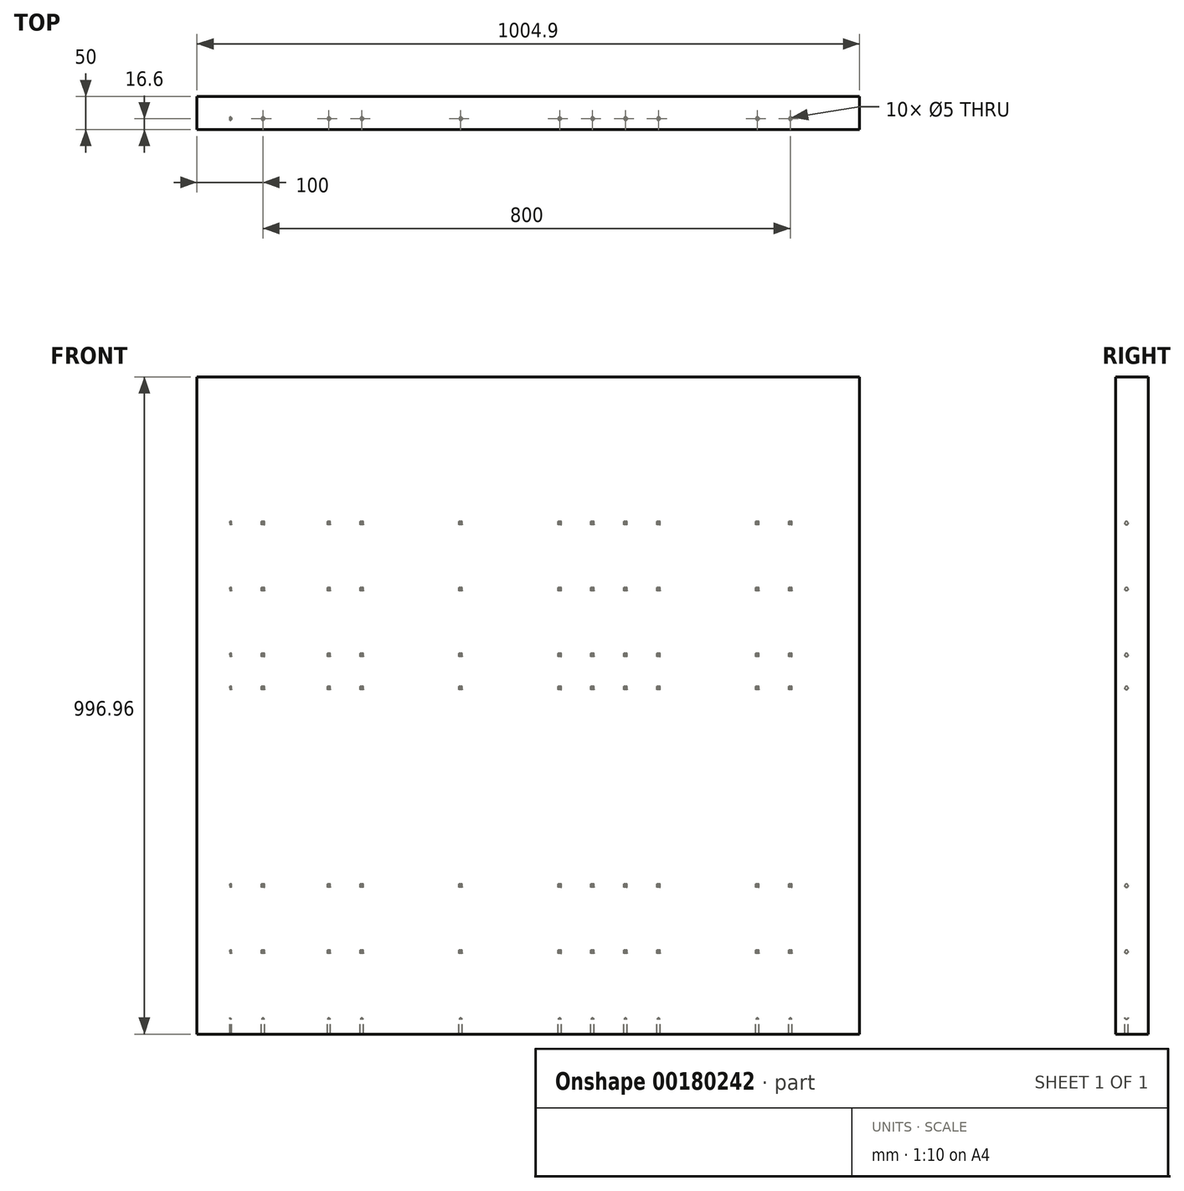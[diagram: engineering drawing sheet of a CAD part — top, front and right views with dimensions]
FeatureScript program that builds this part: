
annotation { "Feature Type Name" : "Feature", "Feature Type Description" : "" }
export const myFeature = defineFeature(function(context is Context, id is Id, definition is map)
    precondition{}
    {
        {
            var Q0;
            Q0=qCreatedBy(makeId("Right.planeOp"),FACE);
            var sketch = newSketch(context, id + "F0", { "sketchPlane" : qUnion([Q0])});
            skLineSegment(sketch, "E0.bottom", {"start": v(25, 491.35) * mm, "end": v(-25, 491.35) * mm});
            skLineSegment(sketch, "E0.top", {"start": v(25, -505.6) * mm, "end": v(-25, -505.6) * mm});
            skLineSegment(sketch, "E0.left", {"start": v(25, 491.35) * mm, "end": v(25, -505.6) * mm});
            skLineSegment(sketch, "E0.right", {"start": v(-25, 491.35) * mm, "end": v(-25, -505.6) * mm});
            skPoint(sketch, "E0.middle", {"position": v(0, -7.13) * mm});
            skLineSegment(sketch, "E1.0", {"start": v(25, -480.6) * mm, "end": v(-25, -480.6) * mm});
            skLineSegment(sketch, "E2.0", {"start": v(-8.4, 542.15) * mm, "end": v(-8.4, -505.6) * mm});
            skCircle(sketch, "E3", {"center": v(-8.4, -480.6) * mm, "radius": 2.5 * mm});
            skCircle(sketch, "E4.0.1.0", {"center": v(-8.4, -430.6) * mm, "radius": 2.5 * mm});
            skCircle(sketch, "E4.0.2.0", {"center": v(-8.4, -380.6) * mm, "radius": 2.5 * mm});
            skCircle(sketch, "E4.0.3.0", {"center": v(-8.4, -330.6) * mm, "radius": 2.5 * mm});
            skCircle(sketch, "E4.0.4.0", {"center": v(-8.4, -280.6) * mm, "radius": 2.5 * mm});
            skCircle(sketch, "E4.0.5.0", {"center": v(-8.4, -230.6) * mm, "radius": 2.5 * mm});
            skCircle(sketch, "E4.0.6.0", {"center": v(-8.4, -180.6) * mm, "radius": 2.5 * mm});
            skCircle(sketch, "E4.0.7.0", {"center": v(-8.4, -130.6) * mm, "radius": 2.5 * mm});
            skCircle(sketch, "E4.0.8.0", {"center": v(-8.4, -80.6) * mm, "radius": 2.5 * mm});
            skCircle(sketch, "E4.0.9.0", {"center": v(-8.4, -30.6) * mm, "radius": 2.5 * mm});
            skCircle(sketch, "E4.0.10.0", {"center": v(-8.4, 19.4) * mm, "radius": 2.5 * mm});
            skCircle(sketch, "E4.0.11.0", {"center": v(-8.4, 69.4) * mm, "radius": 2.5 * mm});
            skCircle(sketch, "E4.0.12.0", {"center": v(-8.4, 119.4) * mm, "radius": 2.5 * mm});
            skCircle(sketch, "E4.0.13.0", {"center": v(-8.4, 169.4) * mm, "radius": 2.5 * mm});
            skCircle(sketch, "E4.0.14.0", {"center": v(-8.4, 219.4) * mm, "radius": 2.5 * mm});
            skCircle(sketch, "E4.0.15.0", {"center": v(-8.4, 269.4) * mm, "radius": 2.5 * mm});
            skCircle(sketch, "E4.0.16.0", {"center": v(-8.4, 319.4) * mm, "radius": 2.5 * mm});
            skCircle(sketch, "E4.0.17.0", {"center": v(-8.4, 369.4) * mm, "radius": 2.5 * mm});
            skCircle(sketch, "E4.0.18.0", {"center": v(-8.4, 419.4) * mm, "radius": 2.5 * mm});
            skLineSegment(sketch, "E4.direction1", {"start": v(-8.4, -480.6) * mm, "end": v(16.6, -480.6) * mm, "construction": true});
            skLineSegment(sketch, "E4.direction2", {"start": v(-8.4, -480.6) * mm, "end": v(-8.4, -430.6) * mm, "construction": true});
            skLineSegment(sketch, "E5", {"start": v(0, 0) * mm, "end": v(63.1, 0) * mm});
            skSolve(sketch);
        }
        {
            var Q0;
            Q0=qCreatedBy(makeId("Top.planeOp"),FACE);
            cPlane(context, id + "F1", {"entities" : qUnion([Q0]), "cplaneType" : CPlaneType.OFFSET, "offset" : 431.2 * mm, "width" : 150 * mm, "height" : 150 * mm});
        }
        {
            var Q0;
            Q0=qCreatedBy(id+"F1.planeOp",FACE);
            var sketch = newSketch(context, id + "F2", { "sketchPlane" : qUnion([Q0])});
            skLineSegment(sketch, "E6.bottom", {"start": v(1004.9, -25) * mm, "end": v(0, -25) * mm});
            skLineSegment(sketch, "E6.top", {"start": v(1004.9, 25) * mm, "end": v(0, 25) * mm});
            skLineSegment(sketch, "E6.left", {"start": v(1004.9, -25) * mm, "end": v(1004.9, 25) * mm});
            skLineSegment(sketch, "E6.right", {"start": v(0, -25) * mm, "end": v(0, 25) * mm});
            skPoint(sketch, "E6.middle", {"position": v(502.45, 0) * mm});
            skLineSegment(sketch, "E7", {"start": v(0, 25) * mm, "end": v(51.84, 25) * mm});
            skLineSegment(sketch, "E8", {"start": v(0, 25) * mm, "end": v(0, 69.64) * mm});
            skLineSegment(sketch, "E9.0", {"start": v(1004.9, -8.4) * mm, "end": v(0, -8.4) * mm});
            skLineSegment(sketch, "E10.0", {"start": v(50, -25) * mm, "end": v(50, 25) * mm});
            skCircle(sketch, "E11", {"center": v(50, -8.4) * mm, "radius": 2.5 * mm});
            skCircle(sketch, "E12.1.0.0", {"center": v(100, -8.4) * mm, "radius": 2.5 * mm});
            skCircle(sketch, "E12.2.0.0", {"center": v(150, -8.4) * mm, "radius": 2.5 * mm});
            skCircle(sketch, "E12.3.0.0", {"center": v(200, -8.4) * mm, "radius": 2.5 * mm});
            skCircle(sketch, "E12.4.0.0", {"center": v(250, -8.4) * mm, "radius": 2.5 * mm});
            skCircle(sketch, "E12.5.0.0", {"center": v(300, -8.4) * mm, "radius": 2.5 * mm});
            skCircle(sketch, "E12.6.0.0", {"center": v(350, -8.4) * mm, "radius": 2.5 * mm});
            skCircle(sketch, "E12.7.0.0", {"center": v(400, -8.4) * mm, "radius": 2.5 * mm});
            skCircle(sketch, "E12.8.0.0", {"center": v(450, -8.4) * mm, "radius": 2.5 * mm});
            skCircle(sketch, "E12.9.0.0", {"center": v(500, -8.4) * mm, "radius": 2.5 * mm});
            skCircle(sketch, "E12.10.0.0", {"center": v(550, -8.4) * mm, "radius": 2.5 * mm});
            skCircle(sketch, "E12.11.0.0", {"center": v(600, -8.4) * mm, "radius": 2.5 * mm});
            skCircle(sketch, "E12.12.0.0", {"center": v(650, -8.4) * mm, "radius": 2.5 * mm});
            skCircle(sketch, "E12.13.0.0", {"center": v(700, -8.4) * mm, "radius": 2.5 * mm});
            skCircle(sketch, "E12.14.0.0", {"center": v(750, -8.4) * mm, "radius": 2.5 * mm});
            skCircle(sketch, "E12.15.0.0", {"center": v(800, -8.4) * mm, "radius": 2.5 * mm});
            skCircle(sketch, "E12.16.0.0", {"center": v(850, -8.4) * mm, "radius": 2.5 * mm});
            skCircle(sketch, "E12.17.0.0", {"center": v(900, -8.4) * mm, "radius": 2.5 * mm});
            skCircle(sketch, "E12.18.0.0", {"center": v(950, -8.4) * mm, "radius": 2.5 * mm});
            skLineSegment(sketch, "E12.direction1", {"start": v(50, -8.4) * mm, "end": v(100, -8.4) * mm, "construction": true});
            skSolve(sketch);
        }
        {
            var Q0;
            {var subQ0=sQuery(id+"F0.wireOp",EDGE,"E4.0.18.0");var subQ1=sQuery(id+"F0.wireOp",EDGE,"E2.0");var subQ2=makeQuery(id+"F0.imprint","INTERSECT",VERTEX,{"disambiguationData":[OD(0.0)],"derivedFrom":[subQ1,subQ0]});Q0=makeQuery(id+"F0.imprint","IMPRINT",FACE,{"disambiguationData":[TD([[makeQuery(id+"F0.imprint","IMPRINT",EDGE,{"disambiguationData":[TD([[subQ2,-1.0]])],"derivedFrom":subQ1}),-1.0]])]});}
            var Q1;
            {var subQ0=sQuery(id+"F0.wireOp",EDGE,"E4.0.19.0");var subQ1=sQuery(id+"F0.wireOp",EDGE,"E2.0");var subQ2=makeQuery(id+"F0.imprint","INTERSECT",VERTEX,{"disambiguationData":[OD(0.0)],"derivedFrom":[subQ1,subQ0]});Q1=makeQuery(id+"F0.imprint","IMPRINT",FACE,{"disambiguationData":[TD([[makeQuery(id+"F0.imprint","IMPRINT",EDGE,{"disambiguationData":[TD([[subQ2,-1.0]])],"derivedFrom":subQ1}),1.0]])]});}
            var Q2;
            {var subQ0=sQuery(id+"F0.wireOp",EDGE,"E4.0.19.0");var subQ1=sQuery(id+"F0.wireOp",EDGE,"E2.0");var subQ2=makeQuery(id+"F0.imprint","INTERSECT",VERTEX,{"disambiguationData":[OD(0.0)],"derivedFrom":[subQ1,subQ0]});Q2=makeQuery(id+"F0.imprint","IMPRINT",FACE,{"disambiguationData":[TD([[makeQuery(id+"F0.imprint","IMPRINT",EDGE,{"disambiguationData":[TD([[subQ2,-1.0]])],"derivedFrom":subQ1}),-1.0]])]});}
            var Q3;
            {var subQ0=sQuery(id+"F0.wireOp",EDGE,"E4.0.17.0");var subQ1=sQuery(id+"F0.wireOp",EDGE,"E2.0");var subQ2=makeQuery(id+"F0.imprint","INTERSECT",VERTEX,{"disambiguationData":[OD(0.0)],"derivedFrom":[subQ1,subQ0]});Q3=makeQuery(id+"F0.imprint","IMPRINT",FACE,{"disambiguationData":[TD([[makeQuery(id+"F0.imprint","IMPRINT",EDGE,{"disambiguationData":[TD([[subQ2,-1.0]])],"derivedFrom":subQ1}),1.0]])]});}
            var Q4;
            {var subQ0=sQuery(id+"F0.wireOp",EDGE,"E4.0.17.0");var subQ1=sQuery(id+"F0.wireOp",EDGE,"E2.0");var subQ2=makeQuery(id+"F0.imprint","INTERSECT",VERTEX,{"disambiguationData":[OD(0.0)],"derivedFrom":[subQ1,subQ0]});Q4=makeQuery(id+"F0.imprint","IMPRINT",FACE,{"disambiguationData":[TD([[makeQuery(id+"F0.imprint","IMPRINT",EDGE,{"disambiguationData":[TD([[subQ2,-1.0]])],"derivedFrom":subQ1}),-1.0]])]});}
            var Q5;
            {var subQ0=sQuery(id+"F0.wireOp",EDGE,"E4.0.18.0");var subQ1=sQuery(id+"F0.wireOp",EDGE,"E2.0");var subQ2=makeQuery(id+"F0.imprint","INTERSECT",VERTEX,{"disambiguationData":[OD(0.0)],"derivedFrom":[subQ1,subQ0]});Q5=makeQuery(id+"F0.imprint","IMPRINT",FACE,{"disambiguationData":[TD([[makeQuery(id+"F0.imprint","IMPRINT",EDGE,{"disambiguationData":[TD([[subQ2,-1.0]])],"derivedFrom":subQ1}),1.0]])]});}
            var Q6;
            {var subQ0=sQuery(id+"F0.wireOp",EDGE,"E4.0.16.0");var subQ1=sQuery(id+"F0.wireOp",EDGE,"E2.0");var subQ2=makeQuery(id+"F0.imprint","INTERSECT",VERTEX,{"disambiguationData":[OD(0.0)],"derivedFrom":[subQ1,subQ0]});Q6=makeQuery(id+"F0.imprint","IMPRINT",FACE,{"disambiguationData":[TD([[makeQuery(id+"F0.imprint","IMPRINT",EDGE,{"disambiguationData":[TD([[subQ2,-1.0]])],"derivedFrom":subQ1}),1.0]])]});}
            var Q7;
            {var subQ0=sQuery(id+"F0.wireOp",EDGE,"E4.0.16.0");var subQ1=sQuery(id+"F0.wireOp",EDGE,"E2.0");var subQ2=makeQuery(id+"F0.imprint","INTERSECT",VERTEX,{"disambiguationData":[OD(0.0)],"derivedFrom":[subQ1,subQ0]});Q7=makeQuery(id+"F0.imprint","IMPRINT",FACE,{"disambiguationData":[TD([[makeQuery(id+"F0.imprint","IMPRINT",EDGE,{"disambiguationData":[TD([[subQ2,-1.0]])],"derivedFrom":subQ1}),-1.0]])]});}
            var Q8;
            {var subQ0=sQuery(id+"F0.wireOp",EDGE,"E4.0.15.0");var subQ1=sQuery(id+"F0.wireOp",EDGE,"E2.0");var subQ2=makeQuery(id+"F0.imprint","INTERSECT",VERTEX,{"disambiguationData":[OD(0.0)],"derivedFrom":[subQ1,subQ0]});Q8=makeQuery(id+"F0.imprint","IMPRINT",FACE,{"disambiguationData":[TD([[makeQuery(id+"F0.imprint","IMPRINT",EDGE,{"disambiguationData":[TD([[subQ2,-1.0]])],"derivedFrom":subQ1}),1.0]])]});}
            var Q9;
            {var subQ0=sQuery(id+"F0.wireOp",EDGE,"E4.0.14.0");var subQ1=sQuery(id+"F0.wireOp",EDGE,"E2.0");var subQ2=makeQuery(id+"F0.imprint","INTERSECT",VERTEX,{"disambiguationData":[OD(0.0)],"derivedFrom":[subQ1,subQ0]});Q9=makeQuery(id+"F0.imprint","IMPRINT",FACE,{"disambiguationData":[TD([[makeQuery(id+"F0.imprint","IMPRINT",EDGE,{"disambiguationData":[TD([[subQ2,-1.0]])],"derivedFrom":subQ1}),-1.0]])]});}
            var Q10;
            {var subQ0=sQuery(id+"F0.wireOp",EDGE,"E4.0.15.0");var subQ1=sQuery(id+"F0.wireOp",EDGE,"E2.0");var subQ2=makeQuery(id+"F0.imprint","INTERSECT",VERTEX,{"disambiguationData":[OD(0.0)],"derivedFrom":[subQ1,subQ0]});Q10=makeQuery(id+"F0.imprint","IMPRINT",FACE,{"disambiguationData":[TD([[makeQuery(id+"F0.imprint","IMPRINT",EDGE,{"disambiguationData":[TD([[subQ2,-1.0]])],"derivedFrom":subQ1}),-1.0]])]});}
            var Q11;
            {var subQ0=sQuery(id+"F0.wireOp",EDGE,"E4.0.13.0");var subQ1=sQuery(id+"F0.wireOp",EDGE,"E2.0");var subQ2=makeQuery(id+"F0.imprint","INTERSECT",VERTEX,{"disambiguationData":[OD(0.0)],"derivedFrom":[subQ1,subQ0]});Q11=makeQuery(id+"F0.imprint","IMPRINT",FACE,{"disambiguationData":[TD([[makeQuery(id+"F0.imprint","IMPRINT",EDGE,{"disambiguationData":[TD([[subQ2,-1.0]])],"derivedFrom":subQ1}),1.0]])]});}
            var Q12;
            {var subQ0=sQuery(id+"F0.wireOp",EDGE,"E4.0.14.0");var subQ1=sQuery(id+"F0.wireOp",EDGE,"E2.0");var subQ2=makeQuery(id+"F0.imprint","INTERSECT",VERTEX,{"disambiguationData":[OD(0.0)],"derivedFrom":[subQ1,subQ0]});Q12=makeQuery(id+"F0.imprint","IMPRINT",FACE,{"disambiguationData":[TD([[makeQuery(id+"F0.imprint","IMPRINT",EDGE,{"disambiguationData":[TD([[subQ2,-1.0]])],"derivedFrom":subQ1}),1.0]])]});}
            var Q13;
            {var subQ0=sQuery(id+"F0.wireOp",EDGE,"E4.0.13.0");var subQ1=sQuery(id+"F0.wireOp",EDGE,"E2.0");var subQ2=makeQuery(id+"F0.imprint","INTERSECT",VERTEX,{"disambiguationData":[OD(0.0)],"derivedFrom":[subQ1,subQ0]});Q13=makeQuery(id+"F0.imprint","IMPRINT",FACE,{"disambiguationData":[TD([[makeQuery(id+"F0.imprint","IMPRINT",EDGE,{"disambiguationData":[TD([[subQ2,-1.0]])],"derivedFrom":subQ1}),-1.0]])]});}
            var Q14;
            {var subQ0=sQuery(id+"F0.wireOp",EDGE,"E4.0.9.0");var subQ1=sQuery(id+"F0.wireOp",EDGE,"E2.0");var subQ2=makeQuery(id+"F0.imprint","INTERSECT",VERTEX,{"disambiguationData":[OD(0.0)],"derivedFrom":[subQ1,subQ0]});Q14=makeQuery(id+"F0.imprint","IMPRINT",FACE,{"disambiguationData":[TD([[makeQuery(id+"F0.imprint","IMPRINT",EDGE,{"disambiguationData":[TD([[subQ2,-1.0]])],"derivedFrom":subQ1}),1.0]])]});}
            var Q15;
            {var subQ0=sQuery(id+"F0.wireOp",EDGE,"E4.0.9.0");var subQ1=sQuery(id+"F0.wireOp",EDGE,"E2.0");var subQ2=makeQuery(id+"F0.imprint","INTERSECT",VERTEX,{"disambiguationData":[OD(0.0)],"derivedFrom":[subQ1,subQ0]});Q15=makeQuery(id+"F0.imprint","IMPRINT",FACE,{"disambiguationData":[TD([[makeQuery(id+"F0.imprint","IMPRINT",EDGE,{"disambiguationData":[TD([[subQ2,-1.0]])],"derivedFrom":subQ1}),-1.0]])]});}
            var Q16;
            {var subQ0=sQuery(id+"F0.wireOp",EDGE,"E4.0.10.0");var subQ1=sQuery(id+"F0.wireOp",EDGE,"E2.0");var subQ2=makeQuery(id+"F0.imprint","INTERSECT",VERTEX,{"disambiguationData":[OD(0.0)],"derivedFrom":[subQ1,subQ0]});Q16=makeQuery(id+"F0.imprint","IMPRINT",FACE,{"disambiguationData":[TD([[makeQuery(id+"F0.imprint","IMPRINT",EDGE,{"disambiguationData":[TD([[subQ2,-1.0]])],"derivedFrom":subQ1}),-1.0]])]});}
            var Q17;
            {var subQ0=sQuery(id+"F0.wireOp",EDGE,"E4.0.12.0");var subQ1=sQuery(id+"F0.wireOp",EDGE,"E2.0");var subQ2=makeQuery(id+"F0.imprint","INTERSECT",VERTEX,{"disambiguationData":[OD(0.0)],"derivedFrom":[subQ1,subQ0]});Q17=makeQuery(id+"F0.imprint","IMPRINT",FACE,{"disambiguationData":[TD([[makeQuery(id+"F0.imprint","IMPRINT",EDGE,{"disambiguationData":[TD([[subQ2,-1.0]])],"derivedFrom":subQ1}),1.0]])]});}
            var Q18;
            {var subQ0=sQuery(id+"F0.wireOp",EDGE,"E4.0.6.0");var subQ1=sQuery(id+"F0.wireOp",EDGE,"E2.0");var subQ2=makeQuery(id+"F0.imprint","INTERSECT",VERTEX,{"disambiguationData":[OD(0.0)],"derivedFrom":[subQ1,subQ0]});Q18=makeQuery(id+"F0.imprint","IMPRINT",FACE,{"disambiguationData":[TD([[makeQuery(id+"F0.imprint","IMPRINT",EDGE,{"disambiguationData":[TD([[subQ2,-1.0]])],"derivedFrom":subQ1}),-1.0]])]});}
            var Q19;
            {var subQ0=sQuery(id+"F0.wireOp",EDGE,"E4.0.11.0");var subQ1=sQuery(id+"F0.wireOp",EDGE,"E2.0");var subQ2=makeQuery(id+"F0.imprint","INTERSECT",VERTEX,{"disambiguationData":[OD(0.0)],"derivedFrom":[subQ1,subQ0]});Q19=makeQuery(id+"F0.imprint","IMPRINT",FACE,{"disambiguationData":[TD([[makeQuery(id+"F0.imprint","IMPRINT",EDGE,{"disambiguationData":[TD([[subQ2,-1.0]])],"derivedFrom":subQ1}),1.0]])]});}
            var Q20;
            {var subQ0=sQuery(id+"F0.wireOp",EDGE,"E4.0.10.0");var subQ1=sQuery(id+"F0.wireOp",EDGE,"E2.0");var subQ2=makeQuery(id+"F0.imprint","INTERSECT",VERTEX,{"disambiguationData":[OD(0.0)],"derivedFrom":[subQ1,subQ0]});Q20=makeQuery(id+"F0.imprint","IMPRINT",FACE,{"disambiguationData":[TD([[makeQuery(id+"F0.imprint","IMPRINT",EDGE,{"disambiguationData":[TD([[subQ2,-1.0]])],"derivedFrom":subQ1}),1.0]])]});}
            var Q21;
            {var subQ0=sQuery(id+"F0.wireOp",EDGE,"E4.0.7.0");var subQ1=sQuery(id+"F0.wireOp",EDGE,"E2.0");var subQ2=makeQuery(id+"F0.imprint","INTERSECT",VERTEX,{"disambiguationData":[OD(0.0)],"derivedFrom":[subQ1,subQ0]});Q21=makeQuery(id+"F0.imprint","IMPRINT",FACE,{"disambiguationData":[TD([[makeQuery(id+"F0.imprint","IMPRINT",EDGE,{"disambiguationData":[TD([[subQ2,-1.0]])],"derivedFrom":subQ1}),-1.0]])]});}
            var Q22;
            {var subQ0=sQuery(id+"F0.wireOp",EDGE,"E4.0.8.0");var subQ1=sQuery(id+"F0.wireOp",EDGE,"E2.0");var subQ2=makeQuery(id+"F0.imprint","INTERSECT",VERTEX,{"disambiguationData":[OD(0.0)],"derivedFrom":[subQ1,subQ0]});Q22=makeQuery(id+"F0.imprint","IMPRINT",FACE,{"disambiguationData":[TD([[makeQuery(id+"F0.imprint","IMPRINT",EDGE,{"disambiguationData":[TD([[subQ2,-1.0]])],"derivedFrom":subQ1}),-1.0]])]});}
            var Q23;
            {var subQ0=sQuery(id+"F0.wireOp",EDGE,"E4.0.11.0");var subQ1=sQuery(id+"F0.wireOp",EDGE,"E2.0");var subQ2=makeQuery(id+"F0.imprint","INTERSECT",VERTEX,{"disambiguationData":[OD(0.0)],"derivedFrom":[subQ1,subQ0]});Q23=makeQuery(id+"F0.imprint","IMPRINT",FACE,{"disambiguationData":[TD([[makeQuery(id+"F0.imprint","IMPRINT",EDGE,{"disambiguationData":[TD([[subQ2,-1.0]])],"derivedFrom":subQ1}),-1.0]])]});}
            var Q24;
            {var subQ0=sQuery(id+"F0.wireOp",EDGE,"E4.0.12.0");var subQ1=sQuery(id+"F0.wireOp",EDGE,"E2.0");var subQ2=makeQuery(id+"F0.imprint","INTERSECT",VERTEX,{"disambiguationData":[OD(0.0)],"derivedFrom":[subQ1,subQ0]});Q24=makeQuery(id+"F0.imprint","IMPRINT",FACE,{"disambiguationData":[TD([[makeQuery(id+"F0.imprint","IMPRINT",EDGE,{"disambiguationData":[TD([[subQ2,-1.0]])],"derivedFrom":subQ1}),-1.0]])]});}
            var Q25;
            {var subQ0=sQuery(id+"F0.wireOp",EDGE,"E4.0.6.0");var subQ1=sQuery(id+"F0.wireOp",EDGE,"E2.0");var subQ2=makeQuery(id+"F0.imprint","INTERSECT",VERTEX,{"disambiguationData":[OD(0.0)],"derivedFrom":[subQ1,subQ0]});Q25=makeQuery(id+"F0.imprint","IMPRINT",FACE,{"disambiguationData":[TD([[makeQuery(id+"F0.imprint","IMPRINT",EDGE,{"disambiguationData":[TD([[subQ2,-1.0]])],"derivedFrom":subQ1}),1.0]])]});}
            var Q26;
            {var subQ0=sQuery(id+"F0.wireOp",EDGE,"E4.0.7.0");var subQ1=sQuery(id+"F0.wireOp",EDGE,"E2.0");var subQ2=makeQuery(id+"F0.imprint","INTERSECT",VERTEX,{"disambiguationData":[OD(0.0)],"derivedFrom":[subQ1,subQ0]});Q26=makeQuery(id+"F0.imprint","IMPRINT",FACE,{"disambiguationData":[TD([[makeQuery(id+"F0.imprint","IMPRINT",EDGE,{"disambiguationData":[TD([[subQ2,-1.0]])],"derivedFrom":subQ1}),1.0]])]});}
            var Q27;
            {var subQ0=sQuery(id+"F0.wireOp",EDGE,"E4.0.8.0");var subQ1=sQuery(id+"F0.wireOp",EDGE,"E2.0");var subQ2=makeQuery(id+"F0.imprint","INTERSECT",VERTEX,{"disambiguationData":[OD(0.0)],"derivedFrom":[subQ1,subQ0]});Q27=makeQuery(id+"F0.imprint","IMPRINT",FACE,{"disambiguationData":[TD([[makeQuery(id+"F0.imprint","IMPRINT",EDGE,{"disambiguationData":[TD([[subQ2,-1.0]])],"derivedFrom":subQ1}),1.0]])]});}
            var Q28;
            {var subQ0=sQuery(id+"F0.wireOp",EDGE,"E4.0.3.0");var subQ1=sQuery(id+"F0.wireOp",EDGE,"E2.0");var subQ2=makeQuery(id+"F0.imprint","INTERSECT",VERTEX,{"disambiguationData":[OD(0.0)],"derivedFrom":[subQ1,subQ0]});Q28=makeQuery(id+"F0.imprint","IMPRINT",FACE,{"disambiguationData":[TD([[makeQuery(id+"F0.imprint","IMPRINT",EDGE,{"disambiguationData":[TD([[subQ2,-1.0]])],"derivedFrom":subQ1}),-1.0]])]});}
            var Q29;
            {var subQ0=sQuery(id+"F0.wireOp",EDGE,"E4.0.4.0");var subQ1=sQuery(id+"F0.wireOp",EDGE,"E2.0");var subQ2=makeQuery(id+"F0.imprint","INTERSECT",VERTEX,{"disambiguationData":[OD(0.0)],"derivedFrom":[subQ1,subQ0]});Q29=makeQuery(id+"F0.imprint","IMPRINT",FACE,{"disambiguationData":[TD([[makeQuery(id+"F0.imprint","IMPRINT",EDGE,{"disambiguationData":[TD([[subQ2,-1.0]])],"derivedFrom":subQ1}),-1.0]])]});}
            var Q30;
            {var subQ0=sQuery(id+"F0.wireOp",EDGE,"E4.0.3.0");var subQ1=sQuery(id+"F0.wireOp",EDGE,"E2.0");var subQ2=makeQuery(id+"F0.imprint","INTERSECT",VERTEX,{"disambiguationData":[OD(0.0)],"derivedFrom":[subQ1,subQ0]});Q30=makeQuery(id+"F0.imprint","IMPRINT",FACE,{"disambiguationData":[TD([[makeQuery(id+"F0.imprint","IMPRINT",EDGE,{"disambiguationData":[TD([[subQ2,-1.0]])],"derivedFrom":subQ1}),1.0]])]});}
            var Q31;
            {var subQ0=sQuery(id+"F0.wireOp",EDGE,"E4.0.5.0");var subQ1=sQuery(id+"F0.wireOp",EDGE,"E2.0");var subQ2=makeQuery(id+"F0.imprint","INTERSECT",VERTEX,{"disambiguationData":[OD(0.0)],"derivedFrom":[subQ1,subQ0]});Q31=makeQuery(id+"F0.imprint","IMPRINT",FACE,{"disambiguationData":[TD([[makeQuery(id+"F0.imprint","IMPRINT",EDGE,{"disambiguationData":[TD([[subQ2,-1.0]])],"derivedFrom":subQ1}),-1.0]])]});}
            var Q32;
            {var subQ0=sQuery(id+"F0.wireOp",EDGE,"E4.0.5.0");var subQ1=sQuery(id+"F0.wireOp",EDGE,"E2.0");var subQ2=makeQuery(id+"F0.imprint","INTERSECT",VERTEX,{"disambiguationData":[OD(0.0)],"derivedFrom":[subQ1,subQ0]});Q32=makeQuery(id+"F0.imprint","IMPRINT",FACE,{"disambiguationData":[TD([[makeQuery(id+"F0.imprint","IMPRINT",EDGE,{"disambiguationData":[TD([[subQ2,-1.0]])],"derivedFrom":subQ1}),1.0]])]});}
            var Q33;
            {var subQ0=sQuery(id+"F0.wireOp",EDGE,"E4.0.2.0");var subQ1=sQuery(id+"F0.wireOp",EDGE,"E2.0");var subQ2=makeQuery(id+"F0.imprint","INTERSECT",VERTEX,{"disambiguationData":[OD(0.0)],"derivedFrom":[subQ1,subQ0]});Q33=makeQuery(id+"F0.imprint","IMPRINT",FACE,{"disambiguationData":[TD([[makeQuery(id+"F0.imprint","IMPRINT",EDGE,{"disambiguationData":[TD([[subQ2,-1.0]])],"derivedFrom":subQ1}),1.0]])]});}
            var Q34;
            {var subQ0=sQuery(id+"F0.wireOp",EDGE,"E4.0.2.0");var subQ1=sQuery(id+"F0.wireOp",EDGE,"E2.0");var subQ2=makeQuery(id+"F0.imprint","INTERSECT",VERTEX,{"disambiguationData":[OD(0.0)],"derivedFrom":[subQ1,subQ0]});Q34=makeQuery(id+"F0.imprint","IMPRINT",FACE,{"disambiguationData":[TD([[makeQuery(id+"F0.imprint","IMPRINT",EDGE,{"disambiguationData":[TD([[subQ2,-1.0]])],"derivedFrom":subQ1}),-1.0]])]});}
            var Q35;
            {var subQ0=sQuery(id+"F0.wireOp",EDGE,"E4.0.4.0");var subQ1=sQuery(id+"F0.wireOp",EDGE,"E2.0");var subQ2=makeQuery(id+"F0.imprint","INTERSECT",VERTEX,{"disambiguationData":[OD(0.0)],"derivedFrom":[subQ1,subQ0]});Q35=makeQuery(id+"F0.imprint","IMPRINT",FACE,{"disambiguationData":[TD([[makeQuery(id+"F0.imprint","IMPRINT",EDGE,{"disambiguationData":[TD([[subQ2,-1.0]])],"derivedFrom":subQ1}),1.0]])]});}
            var Q36;
            {var subQ0=sQuery(id+"F0.wireOp",EDGE,"E4.0.1.0");var subQ1=sQuery(id+"F0.wireOp",EDGE,"E2.0");var subQ2=makeQuery(id+"F0.imprint","INTERSECT",VERTEX,{"disambiguationData":[OD(0.0)],"derivedFrom":[subQ1,subQ0]});Q36=makeQuery(id+"F0.imprint","IMPRINT",FACE,{"disambiguationData":[TD([[makeQuery(id+"F0.imprint","IMPRINT",EDGE,{"disambiguationData":[TD([[subQ2,-1.0]])],"derivedFrom":subQ1}),1.0]])]});}
            var Q37;
            {var subQ0=sQuery(id+"F0.wireOp",EDGE,"E4.0.1.0");var subQ1=sQuery(id+"F0.wireOp",EDGE,"E2.0");var subQ2=makeQuery(id+"F0.imprint","INTERSECT",VERTEX,{"disambiguationData":[OD(0.0)],"derivedFrom":[subQ1,subQ0]});Q37=makeQuery(id+"F0.imprint","IMPRINT",FACE,{"disambiguationData":[TD([[makeQuery(id+"F0.imprint","IMPRINT",EDGE,{"disambiguationData":[TD([[subQ2,-1.0]])],"derivedFrom":subQ1}),-1.0]])]});}
            var Q38;
            {var subQ0=sQuery(id+"F0.wireOp",EDGE,"E2.0");var subQ1=sQuery(id+"F0.wireOp",EDGE,"E1.0");var subQ2=makeQuery(id+"F0.imprint","INTERSECT",VERTEX,{"derivedFrom":[subQ1,subQ0]});Q38=makeQuery(id+"F0.imprint","IMPRINT",FACE,{"disambiguationData":[TD([[makeQuery(id+"F0.imprint","IMPRINT",EDGE,{"disambiguationData":[TD([[subQ2,-1.0]])],"derivedFrom":subQ1}),-1.0]])]});}
            var Q39;
            {var subQ0=sQuery(id+"F0.wireOp",EDGE,"E3");var subQ1=sQuery(id+"F0.wireOp",EDGE,"E1.0");var subQ2=makeQuery(id+"F0.imprint","INTERSECT",VERTEX,{"disambiguationData":[OD(0.0)],"derivedFrom":[subQ1,subQ0]});Q39=makeQuery(id+"F0.imprint","IMPRINT",FACE,{"disambiguationData":[TD([[makeQuery(id+"F0.imprint","IMPRINT",EDGE,{"disambiguationData":[TD([[subQ2,-1.0]])],"derivedFrom":subQ1}),-1.0]])]});}
            var Q40;
            {var subQ0=sQuery(id+"F0.wireOp",EDGE,"E2.0");var subQ1=sQuery(id+"F0.wireOp",EDGE,"E1.0");var subQ2=makeQuery(id+"F0.imprint","INTERSECT",VERTEX,{"derivedFrom":[subQ1,subQ0]});Q40=makeQuery(id+"F0.imprint","IMPRINT",FACE,{"disambiguationData":[TD([[makeQuery(id+"F0.imprint","IMPRINT",EDGE,{"disambiguationData":[TD([[subQ2,-1.0]])],"derivedFrom":subQ1}),1.0]])]});}
            var Q41;
            {var subQ0=sQuery(id+"F0.wireOp",EDGE,"E3");var subQ1=sQuery(id+"F0.wireOp",EDGE,"E1.0");var subQ2=makeQuery(id+"F0.imprint","INTERSECT",VERTEX,{"disambiguationData":[OD(0.0)],"derivedFrom":[subQ1,subQ0]});Q41=makeQuery(id+"F0.imprint","IMPRINT",FACE,{"disambiguationData":[TD([[makeQuery(id+"F0.imprint","IMPRINT",EDGE,{"disambiguationData":[TD([[subQ2,-1.0]])],"derivedFrom":subQ1}),1.0]])]});}
            extrude(context, id + "F3", {"entities" : qUnion([Q0, Q1, Q2, Q3, Q4, Q5, Q6, Q7, Q8, Q9, Q10, Q11, Q12, Q13, Q14, Q15, Q16, Q17, Q18, Q19, Q20, Q21, Q22, Q23, Q24, Q25, Q26, Q27, Q28, Q29, Q30, Q31, Q32, Q33, Q34, Q35, Q36, Q37, Q38, Q39, Q40, Q41]), "depth" : 1004.9 * mm});
        }
        {
            var Q0;
            {var subQ0=sQuery(id+"F2.wireOp",EDGE,"E11");var subQ1=sQuery(id+"F2.wireOp",EDGE,"E9.0");var subQ2=makeQuery(id+"F2.imprint","INTERSECT",VERTEX,{"disambiguationData":[OD(0.0)],"derivedFrom":[subQ1,subQ0]});Q0=makeQuery(id+"F2.imprint","IMPRINT",FACE,{"disambiguationData":[TD([[makeQuery(id+"F2.imprint","IMPRINT",EDGE,{"disambiguationData":[TD([[subQ2,-1.0]])],"derivedFrom":subQ1}),1.0]])]});}
            var Q1;
            {var subQ0=sQuery(id+"F2.wireOp",EDGE,"E10.0");var subQ1=sQuery(id+"F2.wireOp",EDGE,"E9.0");var subQ2=makeQuery(id+"F2.imprint","INTERSECT",VERTEX,{"derivedFrom":[subQ1,subQ0]});Q1=makeQuery(id+"F2.imprint","IMPRINT",FACE,{"disambiguationData":[TD([[makeQuery(id+"F2.imprint","IMPRINT",EDGE,{"disambiguationData":[TD([[subQ2,-1.0]])],"derivedFrom":subQ1}),1.0]])]});}
            var Q2;
            {var subQ0=sQuery(id+"F2.wireOp",EDGE,"E10.0");var subQ1=sQuery(id+"F2.wireOp",EDGE,"E9.0");var subQ2=makeQuery(id+"F2.imprint","INTERSECT",VERTEX,{"derivedFrom":[subQ1,subQ0]});Q2=makeQuery(id+"F2.imprint","IMPRINT",FACE,{"disambiguationData":[TD([[makeQuery(id+"F2.imprint","IMPRINT",EDGE,{"disambiguationData":[TD([[subQ2,-1.0]])],"derivedFrom":subQ1}),-1.0]])]});}
            var Q3;
            {var subQ0=sQuery(id+"F2.wireOp",EDGE,"E11");var subQ1=sQuery(id+"F2.wireOp",EDGE,"E9.0");var subQ2=makeQuery(id+"F2.imprint","INTERSECT",VERTEX,{"disambiguationData":[OD(0.0)],"derivedFrom":[subQ1,subQ0]});Q3=makeQuery(id+"F2.imprint","IMPRINT",FACE,{"disambiguationData":[TD([[makeQuery(id+"F2.imprint","IMPRINT",EDGE,{"disambiguationData":[TD([[subQ2,-1.0]])],"derivedFrom":subQ1}),-1.0]])]});}
            var Q4;
            {var subQ0=sQuery(id+"F2.wireOp",EDGE,"E12.3.0.0");var subQ1=sQuery(id+"F2.wireOp",EDGE,"E9.0");var subQ2=makeQuery(id+"F2.imprint","INTERSECT",VERTEX,{"disambiguationData":[OD(0.0)],"derivedFrom":[subQ1,subQ0]});Q4=makeQuery(id+"F2.imprint","IMPRINT",FACE,{"disambiguationData":[TD([[makeQuery(id+"F2.imprint","IMPRINT",EDGE,{"disambiguationData":[TD([[subQ2,-1.0]])],"derivedFrom":subQ1}),-1.0]])]});}
            var Q5;
            {var subQ0=sQuery(id+"F2.wireOp",EDGE,"E12.2.0.0");var subQ1=sQuery(id+"F2.wireOp",EDGE,"E9.0");var subQ2=makeQuery(id+"F2.imprint","INTERSECT",VERTEX,{"disambiguationData":[OD(0.0)],"derivedFrom":[subQ1,subQ0]});Q5=makeQuery(id+"F2.imprint","IMPRINT",FACE,{"disambiguationData":[TD([[makeQuery(id+"F2.imprint","IMPRINT",EDGE,{"disambiguationData":[TD([[subQ2,-1.0]])],"derivedFrom":subQ1}),-1.0]])]});}
            var Q6;
            {var subQ0=sQuery(id+"F2.wireOp",EDGE,"E12.3.0.0");var subQ1=sQuery(id+"F2.wireOp",EDGE,"E9.0");var subQ2=makeQuery(id+"F2.imprint","INTERSECT",VERTEX,{"disambiguationData":[OD(0.0)],"derivedFrom":[subQ1,subQ0]});Q6=makeQuery(id+"F2.imprint","IMPRINT",FACE,{"disambiguationData":[TD([[makeQuery(id+"F2.imprint","IMPRINT",EDGE,{"disambiguationData":[TD([[subQ2,-1.0]])],"derivedFrom":subQ1}),1.0]])]});}
            var Q7;
            {var subQ0=sQuery(id+"F2.wireOp",EDGE,"E12.2.0.0");var subQ1=sQuery(id+"F2.wireOp",EDGE,"E9.0");var subQ2=makeQuery(id+"F2.imprint","INTERSECT",VERTEX,{"disambiguationData":[OD(0.0)],"derivedFrom":[subQ1,subQ0]});Q7=makeQuery(id+"F2.imprint","IMPRINT",FACE,{"disambiguationData":[TD([[makeQuery(id+"F2.imprint","IMPRINT",EDGE,{"disambiguationData":[TD([[subQ2,-1.0]])],"derivedFrom":subQ1}),1.0]])]});}
            var Q8;
            {var subQ0=sQuery(id+"F2.wireOp",EDGE,"E12.1.0.0");var subQ1=sQuery(id+"F2.wireOp",EDGE,"E9.0");var subQ2=makeQuery(id+"F2.imprint","INTERSECT",VERTEX,{"disambiguationData":[OD(0.0)],"derivedFrom":[subQ1,subQ0]});Q8=makeQuery(id+"F2.imprint","IMPRINT",FACE,{"disambiguationData":[TD([[makeQuery(id+"F2.imprint","IMPRINT",EDGE,{"disambiguationData":[TD([[subQ2,-1.0]])],"derivedFrom":subQ1}),1.0]])]});}
            var Q9;
            {var subQ0=sQuery(id+"F2.wireOp",EDGE,"E12.1.0.0");var subQ1=sQuery(id+"F2.wireOp",EDGE,"E9.0");var subQ2=makeQuery(id+"F2.imprint","INTERSECT",VERTEX,{"disambiguationData":[OD(0.0)],"derivedFrom":[subQ1,subQ0]});Q9=makeQuery(id+"F2.imprint","IMPRINT",FACE,{"disambiguationData":[TD([[makeQuery(id+"F2.imprint","IMPRINT",EDGE,{"disambiguationData":[TD([[subQ2,-1.0]])],"derivedFrom":subQ1}),-1.0]])]});}
            var Q10;
            {var subQ0=sQuery(id+"F2.wireOp",EDGE,"E12.6.0.0");var subQ1=sQuery(id+"F2.wireOp",EDGE,"E9.0");var subQ2=makeQuery(id+"F2.imprint","INTERSECT",VERTEX,{"disambiguationData":[OD(0.0)],"derivedFrom":[subQ1,subQ0]});Q10=makeQuery(id+"F2.imprint","IMPRINT",FACE,{"disambiguationData":[TD([[makeQuery(id+"F2.imprint","IMPRINT",EDGE,{"disambiguationData":[TD([[subQ2,-1.0]])],"derivedFrom":subQ1}),1.0]])]});}
            var Q11;
            {var subQ0=sQuery(id+"F2.wireOp",EDGE,"E12.4.0.0");var subQ1=sQuery(id+"F2.wireOp",EDGE,"E9.0");var subQ2=makeQuery(id+"F2.imprint","INTERSECT",VERTEX,{"disambiguationData":[OD(0.0)],"derivedFrom":[subQ1,subQ0]});Q11=makeQuery(id+"F2.imprint","IMPRINT",FACE,{"disambiguationData":[TD([[makeQuery(id+"F2.imprint","IMPRINT",EDGE,{"disambiguationData":[TD([[subQ2,-1.0]])],"derivedFrom":subQ1}),1.0]])]});}
            var Q12;
            {var subQ0=sQuery(id+"F2.wireOp",EDGE,"E12.5.0.0");var subQ1=sQuery(id+"F2.wireOp",EDGE,"E9.0");var subQ2=makeQuery(id+"F2.imprint","INTERSECT",VERTEX,{"disambiguationData":[OD(0.0)],"derivedFrom":[subQ1,subQ0]});Q12=makeQuery(id+"F2.imprint","IMPRINT",FACE,{"disambiguationData":[TD([[makeQuery(id+"F2.imprint","IMPRINT",EDGE,{"disambiguationData":[TD([[subQ2,-1.0]])],"derivedFrom":subQ1}),1.0]])]});}
            var Q13;
            {var subQ0=sQuery(id+"F2.wireOp",EDGE,"E12.9.0.0");var subQ1=sQuery(id+"F2.wireOp",EDGE,"E9.0");var subQ2=makeQuery(id+"F2.imprint","INTERSECT",VERTEX,{"disambiguationData":[OD(0.0)],"derivedFrom":[subQ1,subQ0]});Q13=makeQuery(id+"F2.imprint","IMPRINT",FACE,{"disambiguationData":[TD([[makeQuery(id+"F2.imprint","IMPRINT",EDGE,{"disambiguationData":[TD([[subQ2,-1.0]])],"derivedFrom":subQ1}),1.0]])]});}
            var Q14;
            {var subQ0=sQuery(id+"F2.wireOp",EDGE,"E12.8.0.0");var subQ1=sQuery(id+"F2.wireOp",EDGE,"E9.0");var subQ2=makeQuery(id+"F2.imprint","INTERSECT",VERTEX,{"disambiguationData":[OD(0.0)],"derivedFrom":[subQ1,subQ0]});Q14=makeQuery(id+"F2.imprint","IMPRINT",FACE,{"disambiguationData":[TD([[makeQuery(id+"F2.imprint","IMPRINT",EDGE,{"disambiguationData":[TD([[subQ2,-1.0]])],"derivedFrom":subQ1}),-1.0]])]});}
            var Q15;
            {var subQ0=sQuery(id+"F2.wireOp",EDGE,"E12.12.0.0");var subQ1=sQuery(id+"F2.wireOp",EDGE,"E9.0");var subQ2=makeQuery(id+"F2.imprint","INTERSECT",VERTEX,{"disambiguationData":[OD(0.0)],"derivedFrom":[subQ1,subQ0]});Q15=makeQuery(id+"F2.imprint","IMPRINT",FACE,{"disambiguationData":[TD([[makeQuery(id+"F2.imprint","IMPRINT",EDGE,{"disambiguationData":[TD([[subQ2,-1.0]])],"derivedFrom":subQ1}),1.0]])]});}
            var Q16;
            {var subQ0=sQuery(id+"F2.wireOp",EDGE,"E12.4.0.0");var subQ1=sQuery(id+"F2.wireOp",EDGE,"E9.0");var subQ2=makeQuery(id+"F2.imprint","INTERSECT",VERTEX,{"disambiguationData":[OD(0.0)],"derivedFrom":[subQ1,subQ0]});Q16=makeQuery(id+"F2.imprint","IMPRINT",FACE,{"disambiguationData":[TD([[makeQuery(id+"F2.imprint","IMPRINT",EDGE,{"disambiguationData":[TD([[subQ2,-1.0]])],"derivedFrom":subQ1}),-1.0]])]});}
            var Q17;
            {var subQ0=sQuery(id+"F2.wireOp",EDGE,"E12.9.0.0");var subQ1=sQuery(id+"F2.wireOp",EDGE,"E9.0");var subQ2=makeQuery(id+"F2.imprint","INTERSECT",VERTEX,{"disambiguationData":[OD(0.0)],"derivedFrom":[subQ1,subQ0]});Q17=makeQuery(id+"F2.imprint","IMPRINT",FACE,{"disambiguationData":[TD([[makeQuery(id+"F2.imprint","IMPRINT",EDGE,{"disambiguationData":[TD([[subQ2,-1.0]])],"derivedFrom":subQ1}),-1.0]])]});}
            var Q18;
            {var subQ0=sQuery(id+"F2.wireOp",EDGE,"E12.11.0.0");var subQ1=sQuery(id+"F2.wireOp",EDGE,"E9.0");var subQ2=makeQuery(id+"F2.imprint","INTERSECT",VERTEX,{"disambiguationData":[OD(0.0)],"derivedFrom":[subQ1,subQ0]});Q18=makeQuery(id+"F2.imprint","IMPRINT",FACE,{"disambiguationData":[TD([[makeQuery(id+"F2.imprint","IMPRINT",EDGE,{"disambiguationData":[TD([[subQ2,-1.0]])],"derivedFrom":subQ1}),1.0]])]});}
            var Q19;
            {var subQ0=sQuery(id+"F2.wireOp",EDGE,"E12.7.0.0");var subQ1=sQuery(id+"F2.wireOp",EDGE,"E9.0");var subQ2=makeQuery(id+"F2.imprint","INTERSECT",VERTEX,{"disambiguationData":[OD(0.0)],"derivedFrom":[subQ1,subQ0]});Q19=makeQuery(id+"F2.imprint","IMPRINT",FACE,{"disambiguationData":[TD([[makeQuery(id+"F2.imprint","IMPRINT",EDGE,{"disambiguationData":[TD([[subQ2,-1.0]])],"derivedFrom":subQ1}),1.0]])]});}
            var Q20;
            {var subQ0=sQuery(id+"F2.wireOp",EDGE,"E12.10.0.0");var subQ1=sQuery(id+"F2.wireOp",EDGE,"E9.0");var subQ2=makeQuery(id+"F2.imprint","INTERSECT",VERTEX,{"disambiguationData":[OD(0.0)],"derivedFrom":[subQ1,subQ0]});Q20=makeQuery(id+"F2.imprint","IMPRINT",FACE,{"disambiguationData":[TD([[makeQuery(id+"F2.imprint","IMPRINT",EDGE,{"disambiguationData":[TD([[subQ2,-1.0]])],"derivedFrom":subQ1}),-1.0]])]});}
            var Q21;
            {var subQ0=sQuery(id+"F2.wireOp",EDGE,"E12.12.0.0");var subQ1=sQuery(id+"F2.wireOp",EDGE,"E9.0");var subQ2=makeQuery(id+"F2.imprint","INTERSECT",VERTEX,{"disambiguationData":[OD(0.0)],"derivedFrom":[subQ1,subQ0]});Q21=makeQuery(id+"F2.imprint","IMPRINT",FACE,{"disambiguationData":[TD([[makeQuery(id+"F2.imprint","IMPRINT",EDGE,{"disambiguationData":[TD([[subQ2,-1.0]])],"derivedFrom":subQ1}),-1.0]])]});}
            var Q22;
            {var subQ0=sQuery(id+"F2.wireOp",EDGE,"E12.8.0.0");var subQ1=sQuery(id+"F2.wireOp",EDGE,"E9.0");var subQ2=makeQuery(id+"F2.imprint","INTERSECT",VERTEX,{"disambiguationData":[OD(0.0)],"derivedFrom":[subQ1,subQ0]});Q22=makeQuery(id+"F2.imprint","IMPRINT",FACE,{"disambiguationData":[TD([[makeQuery(id+"F2.imprint","IMPRINT",EDGE,{"disambiguationData":[TD([[subQ2,-1.0]])],"derivedFrom":subQ1}),1.0]])]});}
            var Q23;
            {var subQ0=sQuery(id+"F2.wireOp",EDGE,"E12.13.0.0");var subQ1=sQuery(id+"F2.wireOp",EDGE,"E9.0");var subQ2=makeQuery(id+"F2.imprint","INTERSECT",VERTEX,{"disambiguationData":[OD(0.0)],"derivedFrom":[subQ1,subQ0]});Q23=makeQuery(id+"F2.imprint","IMPRINT",FACE,{"disambiguationData":[TD([[makeQuery(id+"F2.imprint","IMPRINT",EDGE,{"disambiguationData":[TD([[subQ2,-1.0]])],"derivedFrom":subQ1}),1.0]])]});}
            var Q24;
            {var subQ0=sQuery(id+"F2.wireOp",EDGE,"E12.6.0.0");var subQ1=sQuery(id+"F2.wireOp",EDGE,"E9.0");var subQ2=makeQuery(id+"F2.imprint","INTERSECT",VERTEX,{"disambiguationData":[OD(0.0)],"derivedFrom":[subQ1,subQ0]});Q24=makeQuery(id+"F2.imprint","IMPRINT",FACE,{"disambiguationData":[TD([[makeQuery(id+"F2.imprint","IMPRINT",EDGE,{"disambiguationData":[TD([[subQ2,-1.0]])],"derivedFrom":subQ1}),-1.0]])]});}
            var Q25;
            {var subQ0=sQuery(id+"F2.wireOp",EDGE,"E12.13.0.0");var subQ1=sQuery(id+"F2.wireOp",EDGE,"E9.0");var subQ2=makeQuery(id+"F2.imprint","INTERSECT",VERTEX,{"disambiguationData":[OD(0.0)],"derivedFrom":[subQ1,subQ0]});Q25=makeQuery(id+"F2.imprint","IMPRINT",FACE,{"disambiguationData":[TD([[makeQuery(id+"F2.imprint","IMPRINT",EDGE,{"disambiguationData":[TD([[subQ2,-1.0]])],"derivedFrom":subQ1}),-1.0]])]});}
            var Q26;
            {var subQ0=sQuery(id+"F2.wireOp",EDGE,"E12.10.0.0");var subQ1=sQuery(id+"F2.wireOp",EDGE,"E9.0");var subQ2=makeQuery(id+"F2.imprint","INTERSECT",VERTEX,{"disambiguationData":[OD(0.0)],"derivedFrom":[subQ1,subQ0]});Q26=makeQuery(id+"F2.imprint","IMPRINT",FACE,{"disambiguationData":[TD([[makeQuery(id+"F2.imprint","IMPRINT",EDGE,{"disambiguationData":[TD([[subQ2,-1.0]])],"derivedFrom":subQ1}),1.0]])]});}
            var Q27;
            {var subQ0=sQuery(id+"F2.wireOp",EDGE,"E12.5.0.0");var subQ1=sQuery(id+"F2.wireOp",EDGE,"E9.0");var subQ2=makeQuery(id+"F2.imprint","INTERSECT",VERTEX,{"disambiguationData":[OD(0.0)],"derivedFrom":[subQ1,subQ0]});Q27=makeQuery(id+"F2.imprint","IMPRINT",FACE,{"disambiguationData":[TD([[makeQuery(id+"F2.imprint","IMPRINT",EDGE,{"disambiguationData":[TD([[subQ2,-1.0]])],"derivedFrom":subQ1}),-1.0]])]});}
            var Q28;
            {var subQ0=sQuery(id+"F2.wireOp",EDGE,"E12.7.0.0");var subQ1=sQuery(id+"F2.wireOp",EDGE,"E9.0");var subQ2=makeQuery(id+"F2.imprint","INTERSECT",VERTEX,{"disambiguationData":[OD(0.0)],"derivedFrom":[subQ1,subQ0]});Q28=makeQuery(id+"F2.imprint","IMPRINT",FACE,{"disambiguationData":[TD([[makeQuery(id+"F2.imprint","IMPRINT",EDGE,{"disambiguationData":[TD([[subQ2,-1.0]])],"derivedFrom":subQ1}),-1.0]])]});}
            var Q29;
            {var subQ0=sQuery(id+"F2.wireOp",EDGE,"E12.11.0.0");var subQ1=sQuery(id+"F2.wireOp",EDGE,"E9.0");var subQ2=makeQuery(id+"F2.imprint","INTERSECT",VERTEX,{"disambiguationData":[OD(0.0)],"derivedFrom":[subQ1,subQ0]});Q29=makeQuery(id+"F2.imprint","IMPRINT",FACE,{"disambiguationData":[TD([[makeQuery(id+"F2.imprint","IMPRINT",EDGE,{"disambiguationData":[TD([[subQ2,-1.0]])],"derivedFrom":subQ1}),-1.0]])]});}
            var Q30;
            {var subQ0=sQuery(id+"F2.wireOp",EDGE,"E12.16.0.0");var subQ1=sQuery(id+"F2.wireOp",EDGE,"E9.0");var subQ2=makeQuery(id+"F2.imprint","INTERSECT",VERTEX,{"disambiguationData":[OD(0.0)],"derivedFrom":[subQ1,subQ0]});Q30=makeQuery(id+"F2.imprint","IMPRINT",FACE,{"disambiguationData":[TD([[makeQuery(id+"F2.imprint","IMPRINT",EDGE,{"disambiguationData":[TD([[subQ2,-1.0]])],"derivedFrom":subQ1}),-1.0]])]});}
            var Q31;
            {var subQ0=sQuery(id+"F2.wireOp",EDGE,"E12.15.0.0");var subQ1=sQuery(id+"F2.wireOp",EDGE,"E9.0");var subQ2=makeQuery(id+"F2.imprint","INTERSECT",VERTEX,{"disambiguationData":[OD(0.0)],"derivedFrom":[subQ1,subQ0]});Q31=makeQuery(id+"F2.imprint","IMPRINT",FACE,{"disambiguationData":[TD([[makeQuery(id+"F2.imprint","IMPRINT",EDGE,{"disambiguationData":[TD([[subQ2,-1.0]])],"derivedFrom":subQ1}),1.0]])]});}
            var Q32;
            {var subQ0=sQuery(id+"F2.wireOp",EDGE,"E12.18.0.0");var subQ1=sQuery(id+"F2.wireOp",EDGE,"E9.0");var subQ2=makeQuery(id+"F2.imprint","INTERSECT",VERTEX,{"disambiguationData":[OD(0.0)],"derivedFrom":[subQ1,subQ0]});Q32=makeQuery(id+"F2.imprint","IMPRINT",FACE,{"disambiguationData":[TD([[makeQuery(id+"F2.imprint","IMPRINT",EDGE,{"disambiguationData":[TD([[subQ2,-1.0]])],"derivedFrom":subQ1}),-1.0]])]});}
            var Q33;
            {var subQ0=sQuery(id+"F2.wireOp",EDGE,"E12.17.0.0");var subQ1=sQuery(id+"F2.wireOp",EDGE,"E9.0");var subQ2=makeQuery(id+"F2.imprint","INTERSECT",VERTEX,{"disambiguationData":[OD(0.0)],"derivedFrom":[subQ1,subQ0]});Q33=makeQuery(id+"F2.imprint","IMPRINT",FACE,{"disambiguationData":[TD([[makeQuery(id+"F2.imprint","IMPRINT",EDGE,{"disambiguationData":[TD([[subQ2,-1.0]])],"derivedFrom":subQ1}),-1.0]])]});}
            var Q34;
            {var subQ0=sQuery(id+"F2.wireOp",EDGE,"E12.15.0.0");var subQ1=sQuery(id+"F2.wireOp",EDGE,"E9.0");var subQ2=makeQuery(id+"F2.imprint","INTERSECT",VERTEX,{"disambiguationData":[OD(0.0)],"derivedFrom":[subQ1,subQ0]});Q34=makeQuery(id+"F2.imprint","IMPRINT",FACE,{"disambiguationData":[TD([[makeQuery(id+"F2.imprint","IMPRINT",EDGE,{"disambiguationData":[TD([[subQ2,-1.0]])],"derivedFrom":subQ1}),-1.0]])]});}
            var Q35;
            {var subQ0=sQuery(id+"F2.wireOp",EDGE,"E12.18.0.0");var subQ1=sQuery(id+"F2.wireOp",EDGE,"E9.0");var subQ2=makeQuery(id+"F2.imprint","INTERSECT",VERTEX,{"disambiguationData":[OD(0.0)],"derivedFrom":[subQ1,subQ0]});Q35=makeQuery(id+"F2.imprint","IMPRINT",FACE,{"disambiguationData":[TD([[makeQuery(id+"F2.imprint","IMPRINT",EDGE,{"disambiguationData":[TD([[subQ2,-1.0]])],"derivedFrom":subQ1}),1.0]])]});}
            var Q36;
            {var subQ0=sQuery(id+"F2.wireOp",EDGE,"E12.16.0.0");var subQ1=sQuery(id+"F2.wireOp",EDGE,"E9.0");var subQ2=makeQuery(id+"F2.imprint","INTERSECT",VERTEX,{"disambiguationData":[OD(0.0)],"derivedFrom":[subQ1,subQ0]});Q36=makeQuery(id+"F2.imprint","IMPRINT",FACE,{"disambiguationData":[TD([[makeQuery(id+"F2.imprint","IMPRINT",EDGE,{"disambiguationData":[TD([[subQ2,-1.0]])],"derivedFrom":subQ1}),1.0]])]});}
            var Q37;
            {var subQ0=sQuery(id+"F2.wireOp",EDGE,"E12.14.0.0");var subQ1=sQuery(id+"F2.wireOp",EDGE,"E9.0");var subQ2=makeQuery(id+"F2.imprint","INTERSECT",VERTEX,{"disambiguationData":[OD(0.0)],"derivedFrom":[subQ1,subQ0]});Q37=makeQuery(id+"F2.imprint","IMPRINT",FACE,{"disambiguationData":[TD([[makeQuery(id+"F2.imprint","IMPRINT",EDGE,{"disambiguationData":[TD([[subQ2,-1.0]])],"derivedFrom":subQ1}),1.0]])]});}
            var Q38;
            {var subQ0=sQuery(id+"F2.wireOp",EDGE,"E12.14.0.0");var subQ1=sQuery(id+"F2.wireOp",EDGE,"E9.0");var subQ2=makeQuery(id+"F2.imprint","INTERSECT",VERTEX,{"disambiguationData":[OD(0.0)],"derivedFrom":[subQ1,subQ0]});Q38=makeQuery(id+"F2.imprint","IMPRINT",FACE,{"disambiguationData":[TD([[makeQuery(id+"F2.imprint","IMPRINT",EDGE,{"disambiguationData":[TD([[subQ2,-1.0]])],"derivedFrom":subQ1}),-1.0]])]});}
            var Q39;
            {var subQ0=sQuery(id+"F2.wireOp",EDGE,"E12.17.0.0");var subQ1=sQuery(id+"F2.wireOp",EDGE,"E9.0");var subQ2=makeQuery(id+"F2.imprint","INTERSECT",VERTEX,{"disambiguationData":[OD(0.0)],"derivedFrom":[subQ1,subQ0]});Q39=makeQuery(id+"F2.imprint","IMPRINT",FACE,{"disambiguationData":[TD([[makeQuery(id+"F2.imprint","IMPRINT",EDGE,{"disambiguationData":[TD([[subQ2,-1.0]])],"derivedFrom":subQ1}),1.0]])]});}
            extrude(context, id + "F4", {"entities" : qUnion([Q0, Q1, Q2, Q3, Q4, Q5, Q6, Q7, Q8, Q9, Q10, Q11, Q12, Q13, Q14, Q15, Q16, Q17, Q18, Q19, Q20, Q21, Q22, Q23, Q24, Q25, Q26, Q27, Q28, Q29, Q30, Q31, Q32, Q33, Q34, Q35, Q36, Q37, Q38, Q39]), "operationType" : NewBodyOperationType.ADD, "oppositeDirection" : true, "depth" : 936.8 * mm});
        }
    });
